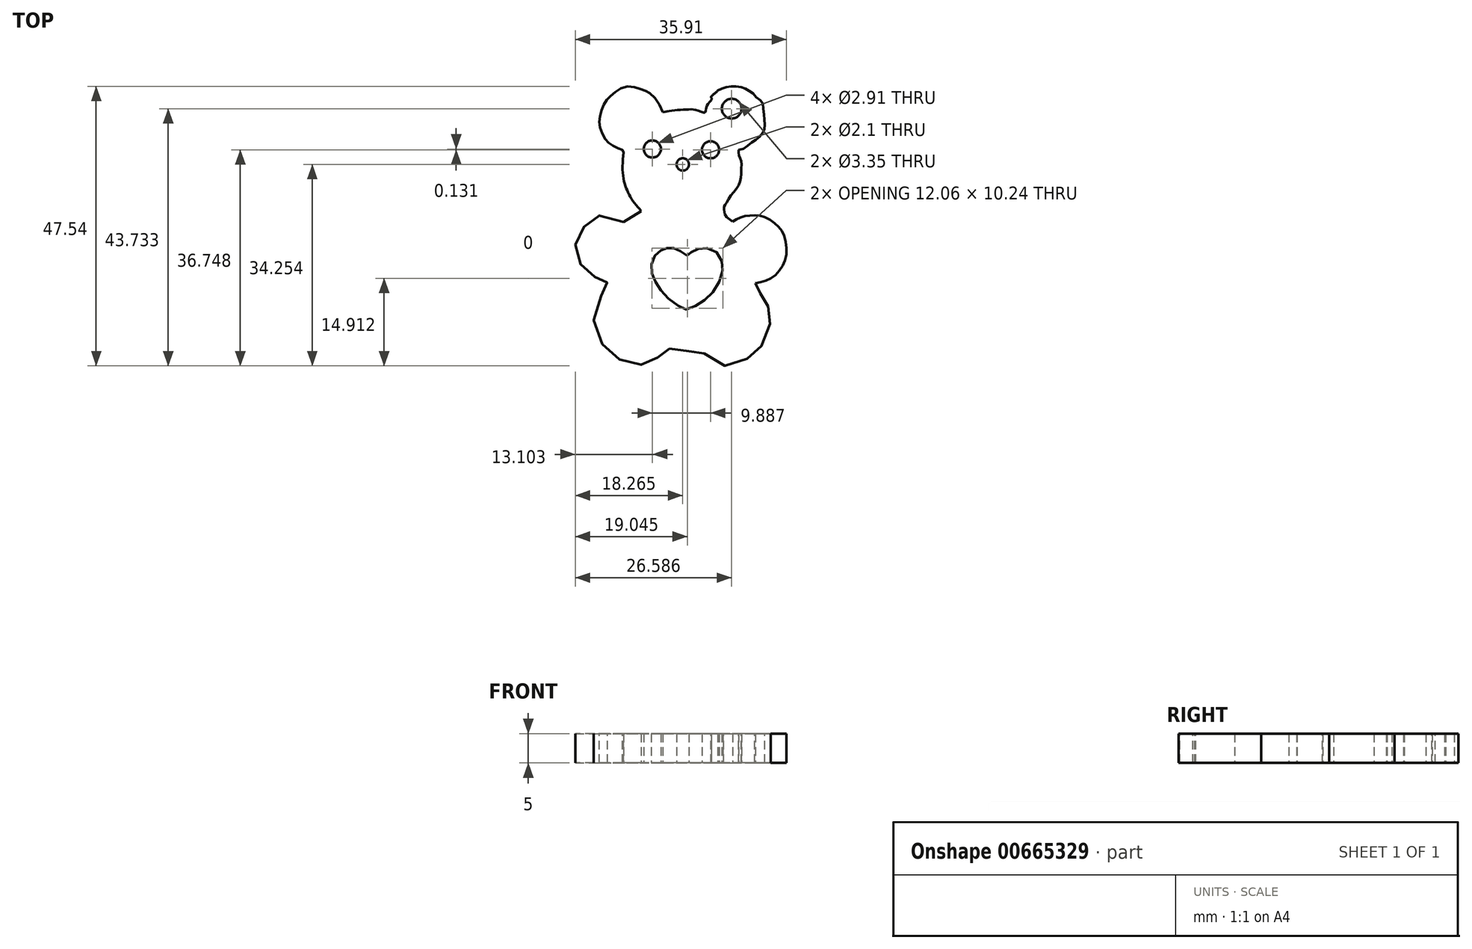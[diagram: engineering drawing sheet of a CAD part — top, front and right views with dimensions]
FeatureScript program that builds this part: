
annotation { "Feature Type Name" : "Feature", "Feature Type Description" : "" }
export const myFeature = defineFeature(function(context is Context, id is Id, definition is map)
    precondition{}
    {
        {
            var Q0;
            Q0=qCreatedBy(makeId("Top.planeOp"),FACE);
            var sketch = newSketch(context, id + "F0", { "sketchPlane" : qUnion([Q0])});
            skFitSpline(sketch, "E0", {"points": [v(12.44, 11.38) * mm, v(13.48, 11.57) * mm, v(15.22, 11.78) * mm, v(16.96, 11.87) * mm, v(18.33, 11.73) * mm, v(19.62, 11.33) * mm, v(19.92, 12.33) * mm, v(20.72, 13.46) * mm], "startDerivative": vector(8, 1.07) * mm, "endDerivative": vector(5, 6.92) * mm});
            skFitSpline(sketch, "E1", {"points": [v(20.72, 13.46) * mm, v(20.7, 13.98) * mm, v(21.83, 15.1) * mm], "startDerivative": vector(1.76, 2.2) * mm, "endDerivative": vector(1.16, 1.9) * mm});
            skFitSpline(sketch, "E2", {"points": [v(21.83, 15.1) * mm, v(22.65, 15.48) * mm, v(23.84, 15.77) * mm, v(24.95, 15.77) * mm, v(26.12, 15.57) * mm, v(26.91, 15.16) * mm, v(27.78, 14.63) * mm, v(28.57, 13.76) * mm, v(29.35, 13.13) * mm, v(29.6, 12.08) * mm, v(29.75, 10.54) * mm, v(29.82, 9.4) * mm, v(29.73, 8.3) * mm, v(29.27, 7.58) * mm, v(28.43, 6.79) * mm, v(27.47, 6.2) * mm, v(26.48, 5.33) * mm, v(25.4, 4.99) * mm], "startDerivative": vector(17.4, 7.38) * mm, "endDerivative": vector(-20.88, -5.98) * mm});
            skFitSpline(sketch, "E3", {"points": [v(25.4, 4.99) * mm, v(25.4, 4.07) * mm, v(25.82, 3.09) * mm, v(25.82, 1.68) * mm, v(25.82, 0.68) * mm, v(25.4, -1.04) * mm, v(24.07, -2.77) * mm, v(23.2, -4.23) * mm, v(22.91, -4.63) * mm, v(23.2, -6.25) * mm, v(24.35, -7.2) * mm], "startDerivative": vector(-1.48, -8.77) * mm, "endDerivative": vector(9.4, -9.66) * mm});
            skFitSpline(sketch, "E4", {"points": [v(24.35, -7.2) * mm, v(25.78, -6.45) * mm, v(27.68, -6.17) * mm, v(29.7, -6.4) * mm, v(31.83, -7.76) * mm, v(33.12, -9.61) * mm, v(33.49, -12.76) * mm, v(32.48, -15.33) * mm, v(30.52, -17.02) * mm, v(28.22, -17.69) * mm], "startDerivative": vector(14.64, 9.4) * mm, "endDerivative": vector(-21, -4.17) * mm});
            skPoint(sketch, "E5.1.internal.orphan", {"position": v(39.54, -39.75) * mm});
            skFitSpline(sketch, "E6", {"points": [v(28.22, -17.69) * mm, v(28.22, -18.7) * mm, v(29, -19.3) * mm, v(29.9, -20.52) * mm, v(30.59, -22.07) * mm, v(30.82, -24.02) * mm, v(29.62, -27.6) * mm, v(28.22, -29.73) * mm, v(25.43, -31.1) * mm, v(22, -31.57) * mm, v(18.86, -29.12) * mm, v(17.44, -29.16) * mm, v(15.65, -29.24) * mm, v(12.97, -28.86) * mm, v(11.9, -29.94) * mm, v(10.7, -30.98) * mm, v(8, -31.57) * mm, v(4.7, -30.36) * mm, v(2.2, -28.04) * mm, v(0.75, -23.98) * mm, v(2.03, -19.85) * mm, v(3, -18.67) * mm, v(2.83, -17.22) * mm, v(1.9, -16.96) * mm, v(0, -16) * mm, v(-1.62, -14.23) * mm, v(-2.38, -11.52) * mm, v(-1.54, -9.09) * mm, v(0, -7.01) * mm, v(2.35, -6.19) * mm, v(6.46, -7.28) * mm, v(8.83, -5.41) * mm], "startDerivative": vector(-10.14, -54.34) * mm, "endDerivative": vector(56.68, 73.9) * mm});
            skFitSpline(sketch, "E7", {"points": [v(8.83, -5.41) * mm, v(7.3, -3.5) * mm, v(6.35, -1.7) * mm, v(5.74, 0.56) * mm, v(5.83, 4.55) * mm], "startDerivative": vector(-6.83, 7.82) * mm, "endDerivative": vector(1.7, 12.98) * mm});
            skFitSpline(sketch, "E8", {"points": [v(5.83, 4.55) * mm, v(5.65, 4.96) * mm, v(4.15, 5.63) * mm, v(2.8, 6.68) * mm, v(1.83, 8.84) * mm, v(1.82, 10.8) * mm, v(2.7, 13.04) * mm, v(3.9, 14.4) * mm, v(6.33, 15.77) * mm, v(8.95, 15.27) * mm, v(10.4, 14.55) * mm, v(12.5, 11.39) * mm], "startDerivative": vector(2.28, 23.97) * mm, "endDerivative": vector(8.34, -30.85) * mm});
            skCircle(sketch, "E9", {"center": v(24.2, 12) * mm, "radius": 1.67 * mm});
            skCircle(sketch, "E10", {"center": v(10.72, 5.14) * mm, "radius": 1.46 * mm});
            skCircle(sketch, "E11", {"center": v(20.61, 5) * mm, "radius": 1.46 * mm});
            skCircle(sketch, "E12", {"center": v(15.89, 2.51) * mm, "radius": 1.05 * mm});
            skFitSpline(sketch, "E13", {"points": [v(13.21, -11.74) * mm, v(12.77, -11.79) * mm, v(12.3, -11.99) * mm, v(11.9, -12.33) * mm, v(11.17, -12.94) * mm, v(10.76, -13.78) * mm, v(10.56, -14.69) * mm, v(10.6, -15.74) * mm, v(10.95, -16.9) * mm, v(11.37, -17.66) * mm, v(11.93, -18.54) * mm, v(12.8, -19.69) * mm, v(13.88, -20.62) * mm, v(15.34, -21.64) * mm, v(16.17, -22) * mm, v(16.6, -22.2) * mm, v(17.9, -21.67) * mm, v(19.02, -20.96) * mm, v(20.29, -19.94) * mm, v(21.25, -18.85) * mm, v(22.14, -17.27) * mm, v(22.64, -15.73) * mm, v(22.67, -14.46) * mm, v(22.48, -13.78) * mm, v(21.86, -12.6) * mm, v(20.4, -11.8) * mm, v(19.7, -11.7) * mm, v(18.77, -11.77) * mm, v(18, -12.05) * mm, v(17.4, -12.33) * mm, v(17.07, -12.73) * mm, v(16.76, -12.85) * mm, v(16.64, -12.97) * mm, v(16.23, -12.63) * mm, v(15.34, -12.17) * mm, v(14.93, -11.9) * mm, v(14.25, -11.68) * mm, v(13.73, -11.61) * mm, v(13.21, -11.74) * mm]});
            skSolve(sketch);
        }
        {
            var Q0;
            {var subQ0=sQuery(id+"F0.wireOp",EDGE,"E1");Q0=makeQuery(id+"F0.imprint","IMPRINT",FACE,{"disambiguationData":[TD([[makeQuery(id+"F0.imprint","IMPRINT",EDGE,{"derivedFrom":subQ0}),-1.0]])]});}
            extrude(context, id + "F1", {"entities" : qUnion([Q0]), "depth" : 5 * mm, "offsetDistance" : 25.4 * mm});
        }
    });
